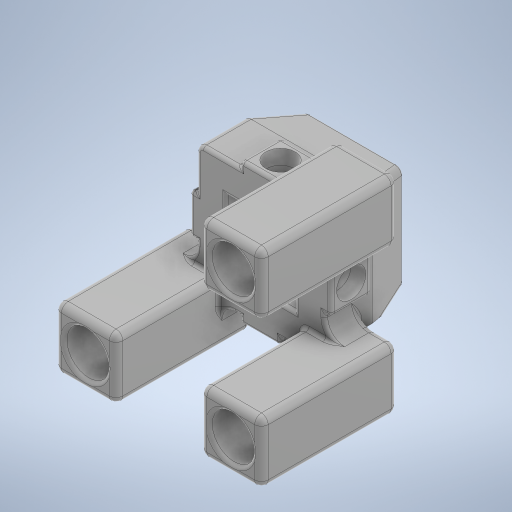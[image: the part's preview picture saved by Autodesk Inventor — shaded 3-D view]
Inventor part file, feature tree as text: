
AUTODESK INVENTOR PART (.ipt)
format: ipt  version: 2023.5 (Build 275446020, 446B)  size: 1,811,456 bytes
history: native  units: mm
features: other x20, extrude x7, fillet x4, projected_geometry x2, chamfer x1, pattern_circular x1
ambient origin geometry x8: Origin, YZ Plane, XZ Plane, XY Plane, X Axis, Y Axis, Z Axis, Center Point
bodies: Solid1 (feature_tree)
feature tree (35):
  other  "Universal_ConstructorHead.ipt"
  other  "NP2_Docking.ipt"
  extrude  "Ex:Side1"  Depth=15.0mm TaperAngle=0.0deg
  other  "Sk:Side2"
  extrude  "Ex:RemoveExcess"  Depth=15.0mm TaperAngle=0.0deg
  extrude  "Ex:Side2"  Depth=15.0mm TaperAngle=0.0deg
  other  "Sk:PostHolder"
  extrude  "Ex:PostHolder"  Depth=15.0mm TaperAngle=0.0deg
  other  "TopCuffPlane"
  fillet  "Fillet:PostHolder1"  Radius=5.0mm
  fillet  "Fillet:PostHolder2"  Radius=10.0mm
  extrude  "Extrusion17"  Depth=10.0mm
  other  "SideSketchPlane"
  other  "Sk:ThreadInsert"
  extrude  "Ex:ThreadHole"  Depth=4.0mm
  extrude  "Ex:ThreadInsert"  TaperAngle=0.0deg  [1 undecoded]
  fillet  "Fillet:ThreadInsert"  [1 undecoded]
  chamfer  "Chamfer:ThreadInsert"  Distance=0.8mm
  pattern_circular  "Pat:ThreadInsert"  [2 undecoded]
  fillet  "Filltet:Final"  Radius=1.15mm
  other  "Sk:Side1"
  other  "TaggingFeature2"
  other  "TaggingFeature4"
  other  "EndPlane_1"
  other  "AnglePlane2"
  other  "AnglePlane1_1"
  other  "FrontPlane"
  other  "SidePlane1"
  other  "SidePlane2"
  projected_geometry  "Projected Loop2"
  projected_geometry  "Projected Loop3"
  other  "Solid1::Universal_ConstructorHead.ipt"
  other  "Srf2"
  other  "Solid1::NP2_Docking.ipt"
  other  "Srf3"
note: 4 required parameter values undecoded (feature->parameter linkage not recoverable at this tier; creation-order binding heuristic only, values carry confidence <= 0.55)
